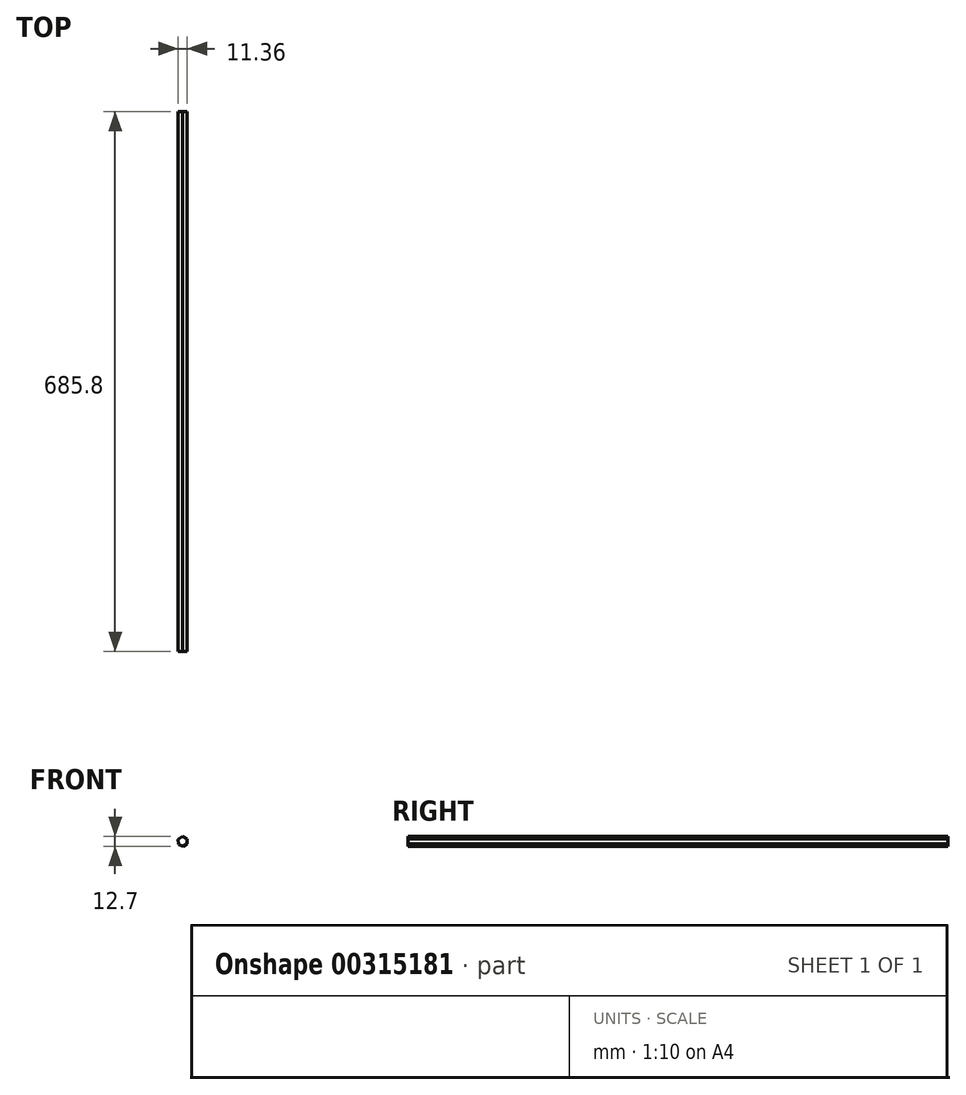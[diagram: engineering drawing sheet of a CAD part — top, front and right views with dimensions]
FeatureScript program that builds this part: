
annotation { "Feature Type Name" : "Feature", "Feature Type Description" : "" }
export const myFeature = defineFeature(function(context is Context, id is Id, definition is map)
    precondition{}
    {
        {
            var Q0;
            Q0=qCreatedBy(makeId("Front.planeOp"),FACE);
            var sketch = newSketch(context, id + "F0", { "sketchPlane" : qUnion([Q0])});
            skCircle(sketch, "E0.cCircle", {"center": v(0, 0) * mm, "radius": 5.5 * mm, "construction": true});
            skLineSegment(sketch, "E0.0", {"start": v(5.68, -2.86) * mm, "end": v(0.36, -6.35) * mm});
            skLineSegment(sketch, "E0.1", {"start": v(0.36, -6.35) * mm, "end": v(-5.32, -3.49) * mm});
            skLineSegment(sketch, "E0.2", {"start": v(-5.32, -3.49) * mm, "end": v(-5.68, 2.86) * mm});
            skLineSegment(sketch, "E0.3", {"start": v(-5.68, 2.86) * mm, "end": v(-0.36, 6.35) * mm});
            skLineSegment(sketch, "E0.4", {"start": v(-0.36, 6.35) * mm, "end": v(5.32, 3.49) * mm});
            skLineSegment(sketch, "E0.5", {"start": v(5.32, 3.49) * mm, "end": v(5.68, -2.86) * mm});
            skPoint(sketch, "E0.0.midPoint", {"position": v(3.02, -4.6) * mm});
            skSolve(sketch);
        }
        {
            var Q0;
            Q0 = qSketchRegion(id + "F0", true);
            extrude(context, id + "F1", {"entities" : qUnion([Q0]), "depth" : 685.8 * mm});
        }
    });
